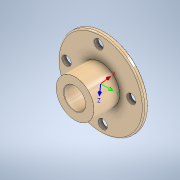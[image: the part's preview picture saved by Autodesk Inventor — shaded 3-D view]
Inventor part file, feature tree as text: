
AUTODESK INVENTOR PART (.ipt)
format: ipt  version: 2021 (Build 250183000, 183)  size: 338,944 bytes
history: native  units: in
note: dims shown in document units (in); Inventor stores cm internally (conversion verified against a paired STEP export)
features: other x12, sketch x7, hole x5, fillet x4, extrude x2
ambient origin geometry x8: Origin, YZ Plane, XZ Plane, XY Plane, X Axis, Y Axis, Z Axis, Center Point
bodies: Solid1 (feature_tree)
feature tree (30):
  extrude  "Extrusion1"  Depth=10.0in TaperAngle=0.0deg
  extrude  "Extrusion2"  Depth=0.125in
  hole  "Hole1"  [1 undecoded]
  hole  "Hole2"  [1 undecoded]
  hole  "Hole3"  [1 undecoded]
  hole  "Hole4"  [1 undecoded]
  hole  "Hole5"  [1 undecoded]
  fillet  "Fillet1"  [1 undecoded]
  fillet  "Fillet2"  [1 undecoded]
  fillet  "Fillet3"  [1 undecoded]
  fillet  "Fillet4"  [1 undecoded]
  other  "UCS1"
  sketch  "Sketch1"  dims[d0=200.0in d1=10.0in d2=0.0in]
  sketch  "Sketch2"  dims[d3=60.0in d4=0.0in]
  sketch  "Sketch3"  dims[d5=10.0in d6=0.024in d7=20.0in d8=10.0in d9=0.5635in d10=1.0in d11=0.8108in]
  sketch  "Sketch4"  dims[d12=10.0in d13=0.024in d14=20.0in d15=10.0in d16=0.5635in d17=1.0in d18=0.8108in]
  sketch  "Sketch5"  dims[d19=10.0in d20=0.024in d21=20.0in d22=10.0in d23=0.5635in d24=1.0in d25=0.8108in]
  sketch  "Sketch6"  dims[d26=10.0in d27=0.024in d28=20.0in d29=10.0in d30=0.5635in d31=1.0in d32=0.8108in]
  sketch  "Sketch7"  dims[d33=10.0in d34=0.024in d35=50.0in d36=100.0in d37=0.5635in d38=1.0in d39=0.8108in d40=0.125in d41=0.125in d42=3.0in d43=1.0in d44=0.0in d45=0.0in d46=0.0in d47=0.0in d48=0.0in d49=0.0in]
  other  "Composite1"
  other  "Composite2"
  other  "UCS1: YZ Plane"
  other  "UCS1: XZ Plane"
  other  "UCS1: XY Plane"
  other  "UCS1: X Axis"
  other  "UCS1: Y Axis"
  other  "UCS1: Z Axis"
  other  "UCS1: Center Point"
  other  "Srf1"
  other  "Srf2"
note: 9 required parameter values undecoded (feature->parameter linkage not recoverable at this tier; creation-order binding heuristic only, values carry confidence <= 0.55)
